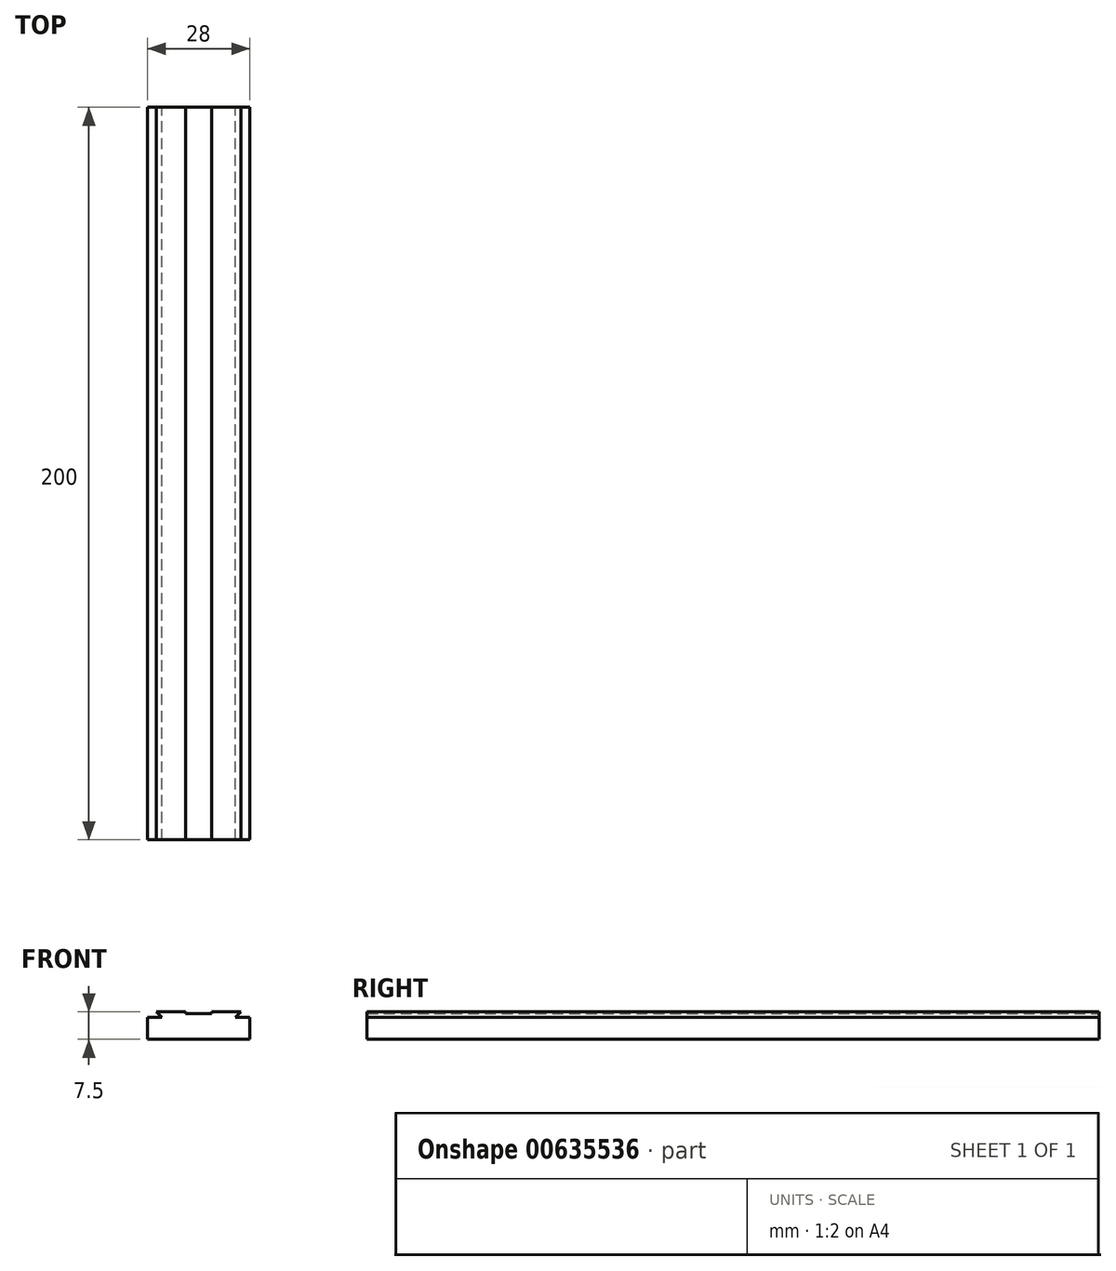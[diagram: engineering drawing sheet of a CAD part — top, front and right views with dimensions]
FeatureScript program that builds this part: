
annotation { "Feature Type Name" : "Feature", "Feature Type Description" : "" }
export const myFeature = defineFeature(function(context is Context, id is Id, definition is map)
    precondition{}
    {
        {
            var Q0;
            Q0=qCreatedBy(makeId("Front.planeOp"),FACE);
            var sketch = newSketch(context, id + "F0", { "sketchPlane" : qUnion([Q0])});
            skLineSegment(sketch, "E0", {"start": v(-14, 0) * mm, "end": v(14, 0) * mm});
            skLineSegment(sketch, "E1", {"start": v(-14, 0) * mm, "end": v(-14, 6) * mm});
            skLineSegment(sketch, "E2", {"start": v(14, 0) * mm, "end": v(14, 6) * mm});
            skLineSegment(sketch, "E3", {"start": v(-14, 6) * mm, "end": v(14, 6) * mm, "construction": true});
            skLineSegment(sketch, "E4", {"start": v(-14, 6) * mm, "end": v(-10, 6) * mm});
            skLineSegment(sketch, "E5", {"start": v(14, 6) * mm, "end": v(10, 6) * mm});
            skLineSegment(sketch, "E6", {"start": v(10, 6) * mm, "end": v(11.5, 7.5) * mm});
            skLineSegment(sketch, "E7", {"start": v(11.5, 7.5) * mm, "end": v(3.5, 7.5) * mm});
            skLineSegment(sketch, "E8", {"start": v(3.5, 7.5) * mm, "end": v(3.5, 7.04) * mm});
            skLineSegment(sketch, "E9", {"start": v(-11.5, 7.5) * mm, "end": v(-10, 6) * mm});
            skLineSegment(sketch, "E10", {"start": v(11.5, 7.5) * mm, "end": v(11.5, 6) * mm, "construction": true});
            skLineSegment(sketch, "E11", {"start": v(-11.5, 7.5) * mm, "end": v(-11.5, 6) * mm, "construction": true});
            skLineSegment(sketch, "E12", {"start": v(-11.5, 7.5) * mm, "end": v(-3.5, 7.5) * mm});
            skLineSegment(sketch, "E13", {"start": v(-3.5, 7.5) * mm, "end": v(-3.5, 7.04) * mm});
            skLineSegment(sketch, "E14", {"start": v(-3.5, 7.04) * mm, "end": v(3.5, 7.04) * mm});
            skSolve(sketch);
        }
        {
            var Q0;
            Q0=makeQuery(id+"F0.imprint","IMPRINT",FACE,{"disambiguationData":[TD([[makeQuery(id+"F0.imprint","IMPRINT",EDGE,{"derivedFrom":sQuery(id+"F0.wireOp",EDGE,"E0")}),1.0]])]});
            extrude(context, id + "F1", {"entities" : qUnion([Q0]), "endBound" : BoundingType.SYMMETRIC, "depth" : 200 * mm, "offsetDistance" : 25 * mm});
        }
    });
